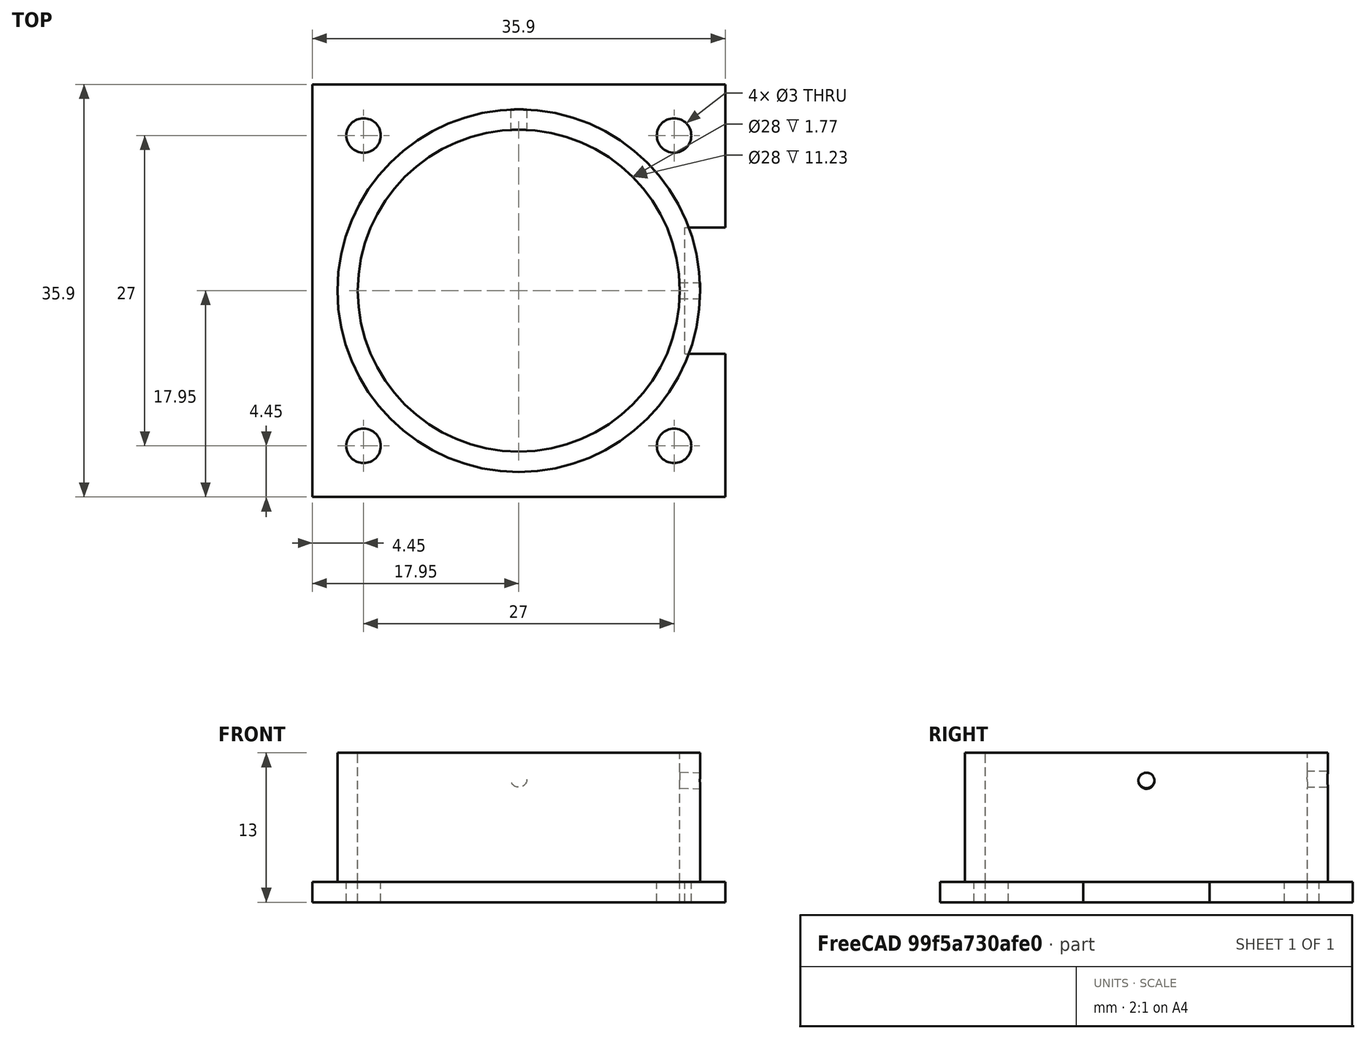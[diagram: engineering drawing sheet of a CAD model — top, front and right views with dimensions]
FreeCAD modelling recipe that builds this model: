
FCSTD DOCUMENT  (FreeCAD 0.16R6706 (Git))
Label: base2
License: All rights reserved
LicenseURL: http://en.wikipedia.org/wiki/All_rights_reserved
objects: Part::Cut×9, Part::Cylinder×8, Part::Box×2, Part::Thickness×1, Part::MultiFuse×1
note: 21 computed .brp shape members not serialized (recipe doc carries the construction recipe); baked Part::Feature solids carry a one-line shape summary decoded from their .brp

FEATURE [Part::Cylinder] Cylinder
  Angle = 360
  Height = 13
  Radius = 14
FEATURE [Part::Box] Box  label="Cube"
  Height = 1.77
  Length = 35.9
  Placement = pos=(-17.95,-17.95,0) rot=(0,0,1;0rad)
  Width = 35.9
FEATURE [Part::Thickness] Thickness
  Faces = -> Cylinder [Face2,Face3]
  Intersection = false
  Join = 0
  Mode = 0
  SelfIntersection = false
  Value = 1.77
FEATURE [Part::Cylinder] Cylinder001
  Angle = 360
  Height = 10
  Placement = pos=(0,0,-3) rot=(0,0,1;0rad)
  Radius = 14
FEATURE [Part::Cylinder] Cylinder002
  Angle = 360
  Height = 10
  Placement = pos=(12,0,10.7) rot=(0,1,0;1.6057rad)
  Radius = 0.7
FEATURE [Part::Cylinder] Cylinder003
  Angle = 360
  Height = 10
  Placement = pos=(13.5,13.5,-2) rot=(0,0,1;0rad)
  Radius = 1.5
FEATURE [Part::Cylinder] Cylinder004
  Angle = 360
  Height = 10
  Placement = pos=(13.5,-13.5,-2) rot=(0,0,1;0rad)
  Radius = 1.5
FEATURE [Part::Cylinder] Cylinder005
  Angle = 360
  Height = 10
  Placement = pos=(-13.5,13.5,-2) rot=(0,0,1;0rad)
  Radius = 1.5
FEATURE [Part::Cylinder] Cylinder006
  Angle = 360
  Height = 10
  Placement = pos=(-13.5,-13.5,-2) rot=(0,0,1;0rad)
  Radius = 1.5
FEATURE [Part::Cylinder] Cylinder007
  Angle = 360
  Height = 10
  Placement = pos=(0,21,10.7) rot=(1,0,0;1.5708rad)
  Radius = 0.7
FEATURE [Part::Cut] Cut
  Base = -> Box
  Tool = -> Cylinder001
FEATURE [Part::Cut] Cut001
  Base = -> Cut
  Tool = -> Cylinder006
FEATURE [Part::Cut] Cut002
  Base = -> Cut001
  Tool = -> Cylinder005
FEATURE [Part::Cut] Cut003
  Base = -> Cut002
  Tool = -> Cylinder004
FEATURE [Part::Cut] Cut004
  Base = -> Cut003
  Tool = -> Cylinder003
FEATURE [Part::Cut] Cut005
  Base = -> Thickness
  Tool = -> Cylinder007
FEATURE [Part::Cut] Cut006
  Base = -> Cut005
  Tool = -> Cylinder002
FEATURE [Part::Box] Box001  label="Cube001"
  Height = 1.77
  Length = 3.5
  Placement = pos=(14.45,-5.5,0) rot=(0,0,1;0rad)
  Width = 11
FEATURE [Part::Cut] Cut007  label="bottom_plate"
  Base = -> Cut004
  Tool = -> Box001
FEATURE [Part::Cut] Cut008  label="lens_conduit"
  Base = -> Cut006
  Tool = -> Box001
FEATURE [Part::MultiFuse] Fusion
  Shapes = -> [Cut007,Cut008]
